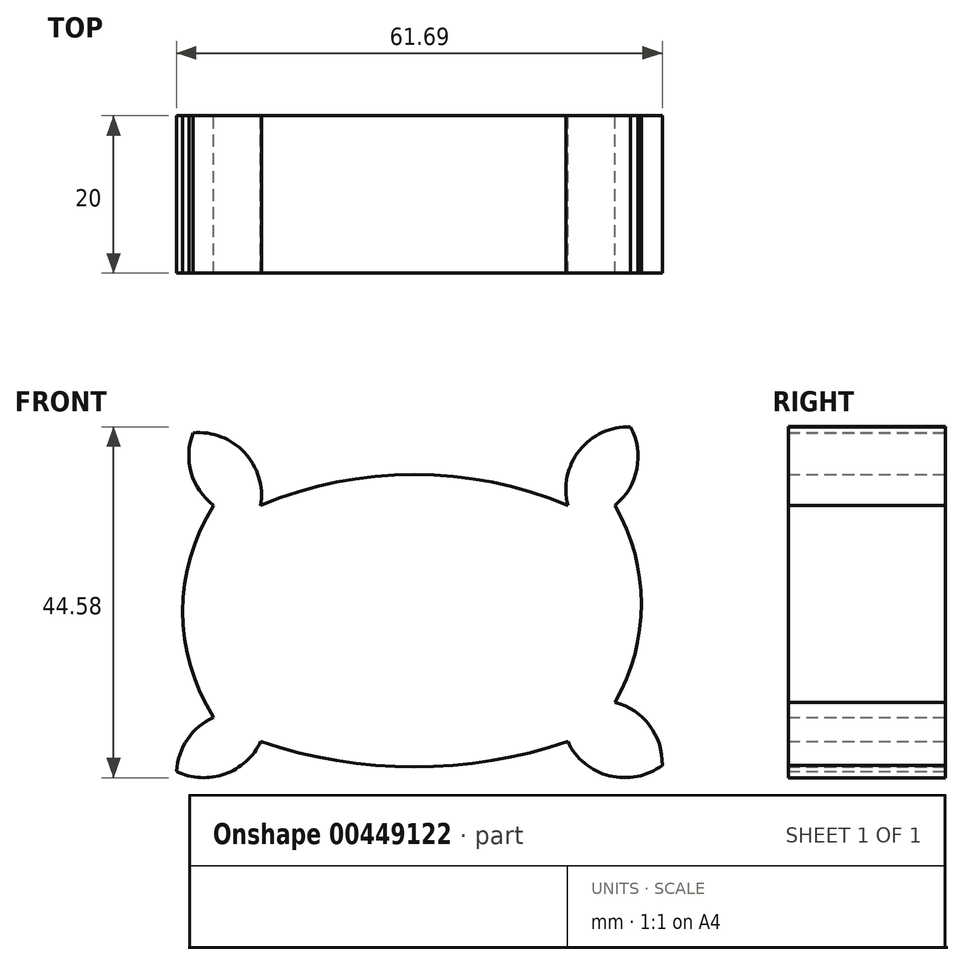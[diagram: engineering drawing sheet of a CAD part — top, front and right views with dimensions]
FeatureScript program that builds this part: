
annotation { "Feature Type Name" : "Feature", "Feature Type Description" : "" }
export const myFeature = defineFeature(function(context is Context, id is Id, definition is map)
    precondition{}
    {
        {
            var Q0;
            Q0=qCreatedBy(makeId("Front.planeOp"),FACE);
            var sketch = newSketch(context, id + "F0", { "sketchPlane" : qUnion([Q0])});
            skArc(sketch, "E0", {"start": v(0, -25) * mm, "mid": v(3.35, -12.5) * mm, "end": v(0, 0) * mm});
            skArc(sketch, "E1", {"start": v(6, -33) * mm, "mid": v(4.4, -27.95) * mm, "end": v(0, -25) * mm});
            skArc(sketch, "E2", {"start": v(-45, -30) * mm, "mid": v(-25.5, -33.22) * mm, "end": v(-6, -30) * mm});
            skPoint(sketch, "E3.startSnap0", {"position": v(-25.5, -33.22) * mm});
            skArc(sketch, "E4", {"start": v(-50.98, 0) * mm, "mid": v(-54.9, -13.45) * mm, "end": v(-50.98, -26.9) * mm});
            skArc(sketch, "E5", {"start": v(0, 0) * mm, "mid": v(2.78, 4.65) * mm, "end": v(1.96, 10) * mm});
            skArc(sketch, "E6", {"start": v(1.96, 10) * mm, "mid": v(-4.52, 6.98) * mm, "end": v(-6, 0) * mm});
            skArc(sketch, "E7", {"start": v(-53.6, 9.22) * mm, "mid": v(-53.83, 4.17) * mm, "end": v(-50.98, 0) * mm});
            skArc(sketch, "E8", {"start": v(-45, 0) * mm, "mid": v(-47.05, 6.71) * mm, "end": v(-53.6, 9.22) * mm});
            skArc(sketch, "E9", {"start": v(-6, 0) * mm, "mid": v(-25.5, 3.94) * mm, "end": v(-45, 0) * mm});
            skArc(sketch, "E10", {"start": v(-55.69, -33.8) * mm, "mid": v(-49.56, -34.12) * mm, "end": v(-45, -30) * mm});
            skArc(sketch, "E11", {"start": v(-50.98, -26.9) * mm, "mid": v(-54.3, -29.69) * mm, "end": v(-55.69, -33.8) * mm});
            skArc(sketch, "E12", {"start": v(-6, -30) * mm, "mid": v(-0.7, -34.34) * mm, "end": v(6, -33) * mm});
            skSolve(sketch);
        }
        {
            var Q0;
            Q0=makeQuery(id+"F0.imprint","IMPRINT",FACE,{"disambiguationData":[TD([[makeQuery(id+"F0.imprint","IMPRINT",EDGE,{"derivedFrom":sQuery(id+"F0.wireOp",EDGE,"E0")}),1.0]])]});
            extrude(context, id + "F1", {"entities" : qUnion([Q0]), "depth" : 20 * mm});
        }
    });
